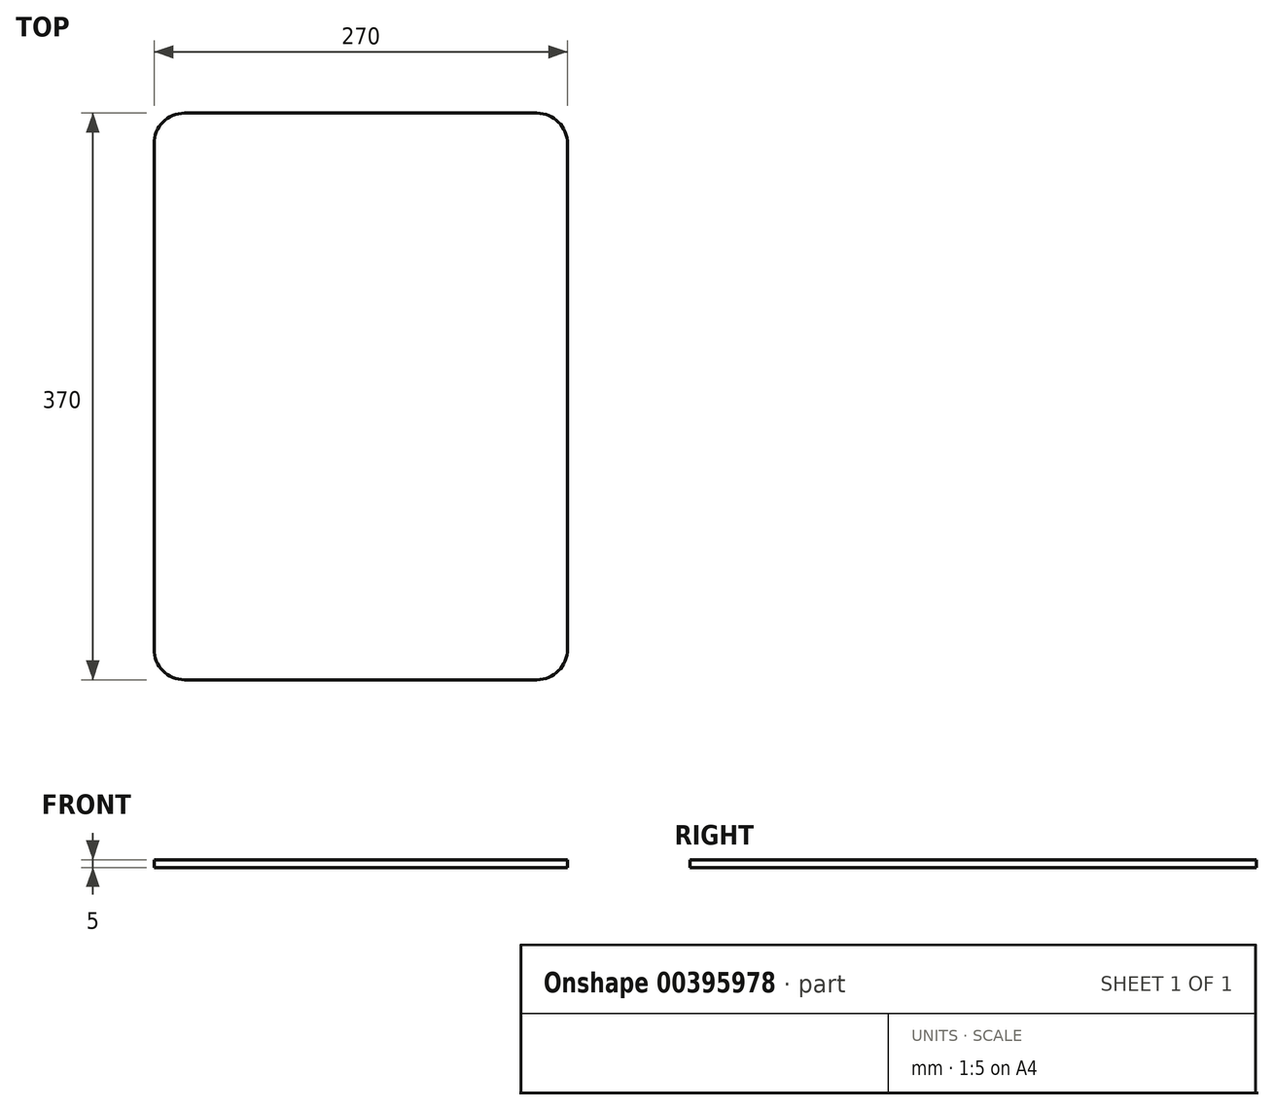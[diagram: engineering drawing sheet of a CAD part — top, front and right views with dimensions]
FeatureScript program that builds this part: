
annotation { "Feature Type Name" : "Feature", "Feature Type Description" : "" }
export const myFeature = defineFeature(function(context is Context, id is Id, definition is map)
    precondition{}
    {
        {
            var Q0;
            Q0=qCreatedBy(makeId("Top.planeOp"),FACE);
            var sketch = newSketch(context, id + "F0", { "sketchPlane" : qUnion([Q0])});
            skLineSegment(sketch, "E0.bottom", {"start": v(115, -185) * mm, "end": v(-115, -185) * mm});
            skLineSegment(sketch, "E0.top", {"start": v(115, 185) * mm, "end": v(-115, 185) * mm});
            skLineSegment(sketch, "E0.left", {"start": v(135, -165) * mm, "end": v(135, 165) * mm});
            skLineSegment(sketch, "E0.right", {"start": v(-135, -165) * mm, "end": v(-135, 165) * mm});
            skPoint(sketch, "E0.middle", {"position": v(0, 0) * mm});
            skPoint(sketch, "E1.visualSharp", {"position": v(-135, -185) * mm});
            skArc(sketch, "E1.filletArc", {"start": v(-135, -165) * mm, "mid": v(-129.14, -179.14) * mm, "end": v(-115, -185) * mm});
            skPoint(sketch, "E2.visualSharp", {"position": v(-135, 185) * mm});
            skArc(sketch, "E2.filletArc", {"start": v(-115, 185) * mm, "mid": v(-129.14, 179.14) * mm, "end": v(-135, 165) * mm});
            skPoint(sketch, "E3.visualSharp", {"position": v(135, 185) * mm});
            skArc(sketch, "E3.filletArc", {"start": v(135, 165) * mm, "mid": v(129.14, 179.14) * mm, "end": v(115, 185) * mm});
            skPoint(sketch, "E4.visualSharp", {"position": v(135, -185) * mm});
            skArc(sketch, "E4.filletArc", {"start": v(115, -185) * mm, "mid": v(129.14, -179.14) * mm, "end": v(135, -165) * mm});
            skSolve(sketch);
        }
        {
            var Q0;
            Q0 = qSketchRegion(id + "F0", true);
            extrude(context, id + "F1", {"entities" : qUnion([Q0]), "depth" : 5 * mm});
        }
    });
